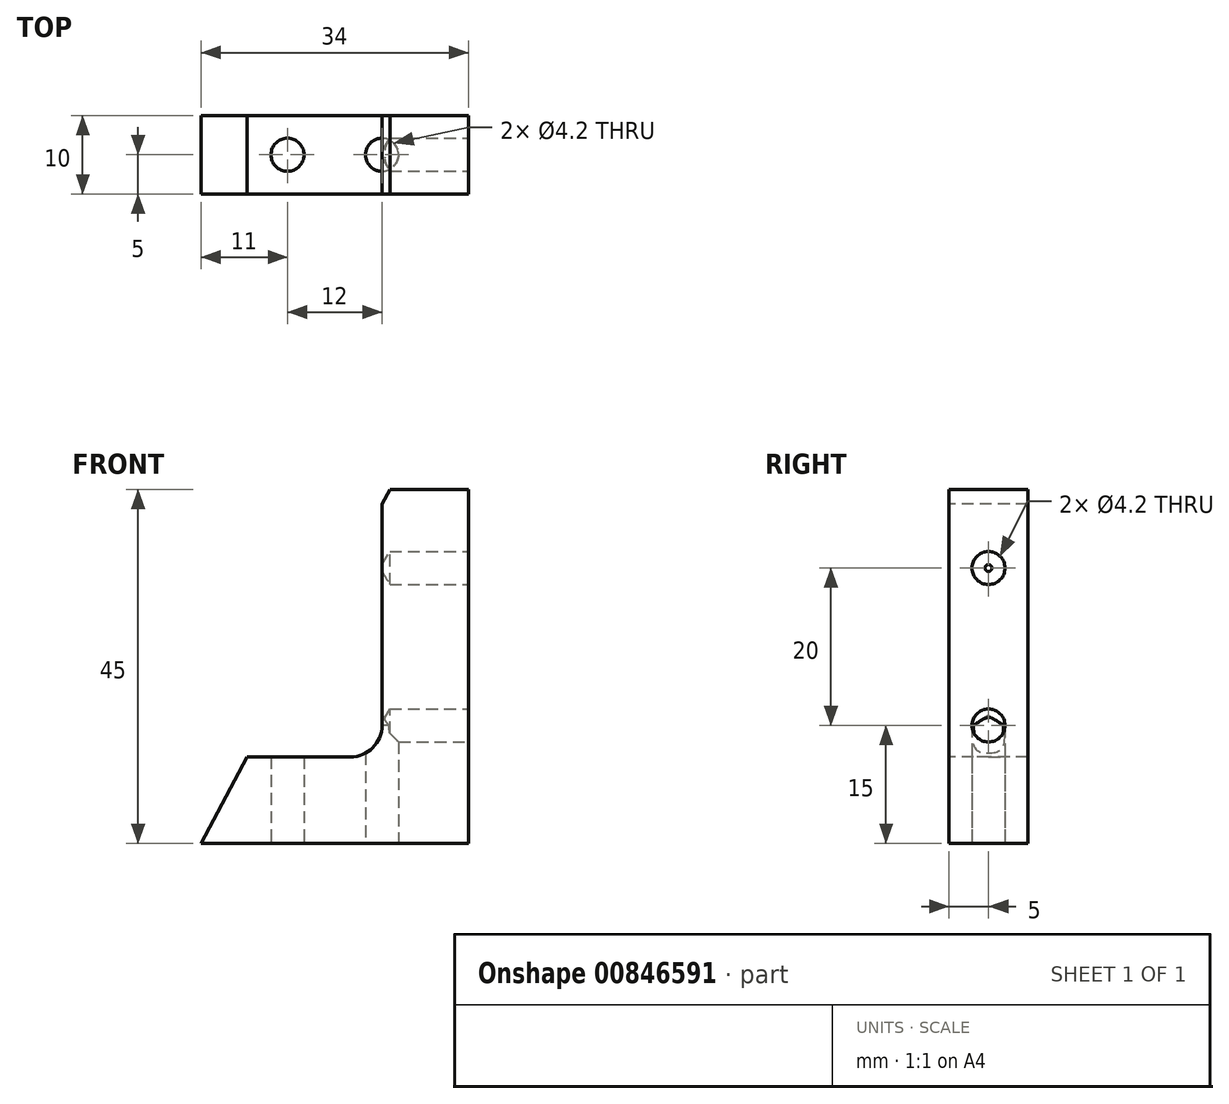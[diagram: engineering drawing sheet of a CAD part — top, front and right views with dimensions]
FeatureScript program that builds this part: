
annotation { "Feature Type Name" : "Feature", "Feature Type Description" : "" }
export const myFeature = defineFeature(function(context is Context, id is Id, definition is map)
    precondition{}
    {
        {
            var Q0;
            Q0=qCreatedBy(makeId("Front.planeOp"),FACE);
            var sketch = newSketch(context, id + "F0", { "sketchPlane" : qUnion([Q0])});
            skLineSegment(sketch, "E0", {"start": v(0, 0) * mm, "end": v(34, 0) * mm});
            skLineSegment(sketch, "E1", {"start": v(34, 0) * mm, "end": v(34, 45) * mm});
            skLineSegment(sketch, "E2", {"start": v(34, 45) * mm, "end": v(24, 45) * mm});
            skLineSegment(sketch, "E3", {"start": v(24, 45) * mm, "end": v(0, 0) * mm});
            skSolve(sketch);
        }
        {
            var Q0;
            Q0=makeQuery(id+"F0.imprint","IMPRINT",FACE,{"disambiguationData":[TD([[makeQuery(id+"F0.imprint","IMPRINT",EDGE,{"derivedFrom":sQuery(id+"F0.wireOp",EDGE,"E0")}),1.0]])]});
            extrude(context, id + "F1", {"entities" : qUnion([Q0]), "depth" : 10 * mm, "offsetDistance" : 25 * mm});
        }
        {
            var Q0;
            Q0=makeQuery(id+"F1.opExtrude","SWEPT_FACE",FACE,{"disambiguationData":[OSD([sQuery(id+"F0.wireOp",EDGE,"E0")])]});
            var sketch = newSketch(context, id + "F2", { "sketchPlane" : qUnion([Q0])});
            skPoint(sketch, "E4", {"position": v(34, 5) * mm});
            skPoint(sketch, "E5", {"position": v(23, 5) * mm});
            skPoint(sketch, "E6", {"position": v(11, 5) * mm});
            skSolve(sketch);
        }
        {
            var Q0;
            Q0=sQuery(id+"F2.wireOp",VERTEX,"E5");
            var Q1;
            Q1=sQuery(id+"F2.wireOp",VERTEX,"E6");
            var Q2;
            Q2=makeQuery(id+"F1.opExtrude","SWEPT_BODY",BODY,{"disambiguationData":[OSD([sQuery(id+"F0.wireOp",EDGE,"E0"),sQuery(id+"F0.wireOp",EDGE,"E1"),sQuery(id+"F0.wireOp",EDGE,"E2"),sQuery(id+"F0.wireOp",EDGE,"E3")])]});
            hole(context, id + "F3", {"style" : HoleStyle.SIMPLE, "endStyle" : HoleEndStyle.BLIND, "standardTappedOrClearance" : lookupTablePath({ "standard" : "ISO", "engagement" : "75%", "pitch" : "0.8 mm", "size" : "M5", "type" : "Tapped" }), "standardBlindInLast" : lookupTablePath({ "standard" : "ISO", "engagement" : "75%", "pitch" : "0.8 mm", "size" : "M5", "type" : "Tapped" }), "holeDiameter" : 4.2 * mm, "majorDiameter" : 5 * mm, "showTappedDepth" : true, "holeDepth" : 15 * mm, "isTappedThrough" : true, "tappedDepth" : 12.6 * mm, "tapClearance" : 3, "locations" : qUnion([Q0, Q1]), "scope" : qUnion([Q2])});
        }
        {
            var Q0;
            Q0=makeQuery(id+"F1.opExtrude","SWEPT_FACE",FACE,{"disambiguationData":[OSD([sQuery(id+"F0.wireOp",EDGE,"E1")])]});
            var sketch = newSketch(context, id + "F4", { "sketchPlane" : qUnion([Q0])});
            skPoint(sketch, "E7", {"position": v(-5, 15) * mm});
            skPoint(sketch, "E7.positionSnap0", {"position": v(-5, 0) * mm});
            skPoint(sketch, "E8", {"position": v(-5, 35) * mm});
            skSolve(sketch);
        }
        {
            var Q0;
            Q0=sQuery(id+"F4.wireOp",VERTEX,"E8");
            var Q1;
            Q1=sQuery(id+"F4.wireOp",VERTEX,"E7");
            var Q2;
            Q2=makeQuery(id+"F1.opExtrude","SWEPT_BODY",BODY,{"disambiguationData":[OSD([sQuery(id+"F0.wireOp",EDGE,"E0"),sQuery(id+"F0.wireOp",EDGE,"E1"),sQuery(id+"F0.wireOp",EDGE,"E2"),sQuery(id+"F0.wireOp",EDGE,"E3")])]});
            hole(context, id + "F5", {"style" : HoleStyle.SIMPLE, "endStyle" : HoleEndStyle.BLIND, "standardTappedOrClearance" : lookupTablePath({ "standard" : "ISO", "engagement" : "75%", "pitch" : "0.8 mm", "size" : "M5", "type" : "Tapped" }), "standardBlindInLast" : lookupTablePath({ "standard" : "ISO", "engagement" : "75%", "pitch" : "0.8 mm", "size" : "M5", "type" : "Tapped" }), "holeDiameter" : 4.2 * mm, "majorDiameter" : 5 * mm, "showTappedDepth" : true, "holeDepth" : 10 * mm, "isTappedThrough" : true, "tappedDepth" : 7.6 * mm, "tapClearance" : 3, "locations" : qUnion([Q0, Q1]), "scope" : qUnion([Q2])});
        }
        {
            var Q0;
            Q0=makeQuery(id+"F1.opExtrude","CAP_FACE",FACE,{"disambiguationData":[OSD([sQuery(id+"F0.wireOp",EDGE,"E0"),sQuery(id+"F0.wireOp",EDGE,"E1"),sQuery(id+"F0.wireOp",EDGE,"E2"),sQuery(id+"F0.wireOp",EDGE,"E3")])],"isStart":false});
            var sketch = newSketch(context, id + "F6", { "sketchPlane" : qUnion([Q0])});
            skPoint(sketch, "E9", {"position": v(19, 15) * mm});
            skCircle(sketch, "E10", {"center": v(19, 15) * mm, "radius": 4 * mm});
            skCircle(sketch, "E11", {"center": v(0, 15) * mm, "radius": 2.47 * mm});
            skLineSegment(sketch, "E12", {"start": v(23, 15) * mm, "end": v(23, 43.12) * mm});
            skLineSegment(sketch, "E13", {"start": v(19, 11) * mm, "end": v(5.87, 11) * mm});
            skLineSegment(sketch, "E14", {"start": v(23, 43.12) * mm, "end": v(5.87, 11) * mm});
            skSolve(sketch);
        }
        {
            var Q0;
            Q0 = qSketchRegion(id + "F6", true);
            extrude(context, id + "F7", {"entities" : qUnion([Q0]), "operationType" : NewBodyOperationType.REMOVE, "oppositeDirection" : true, "depth" : 25 * mm, "offsetDistance" : 25 * mm});
        }
    });
